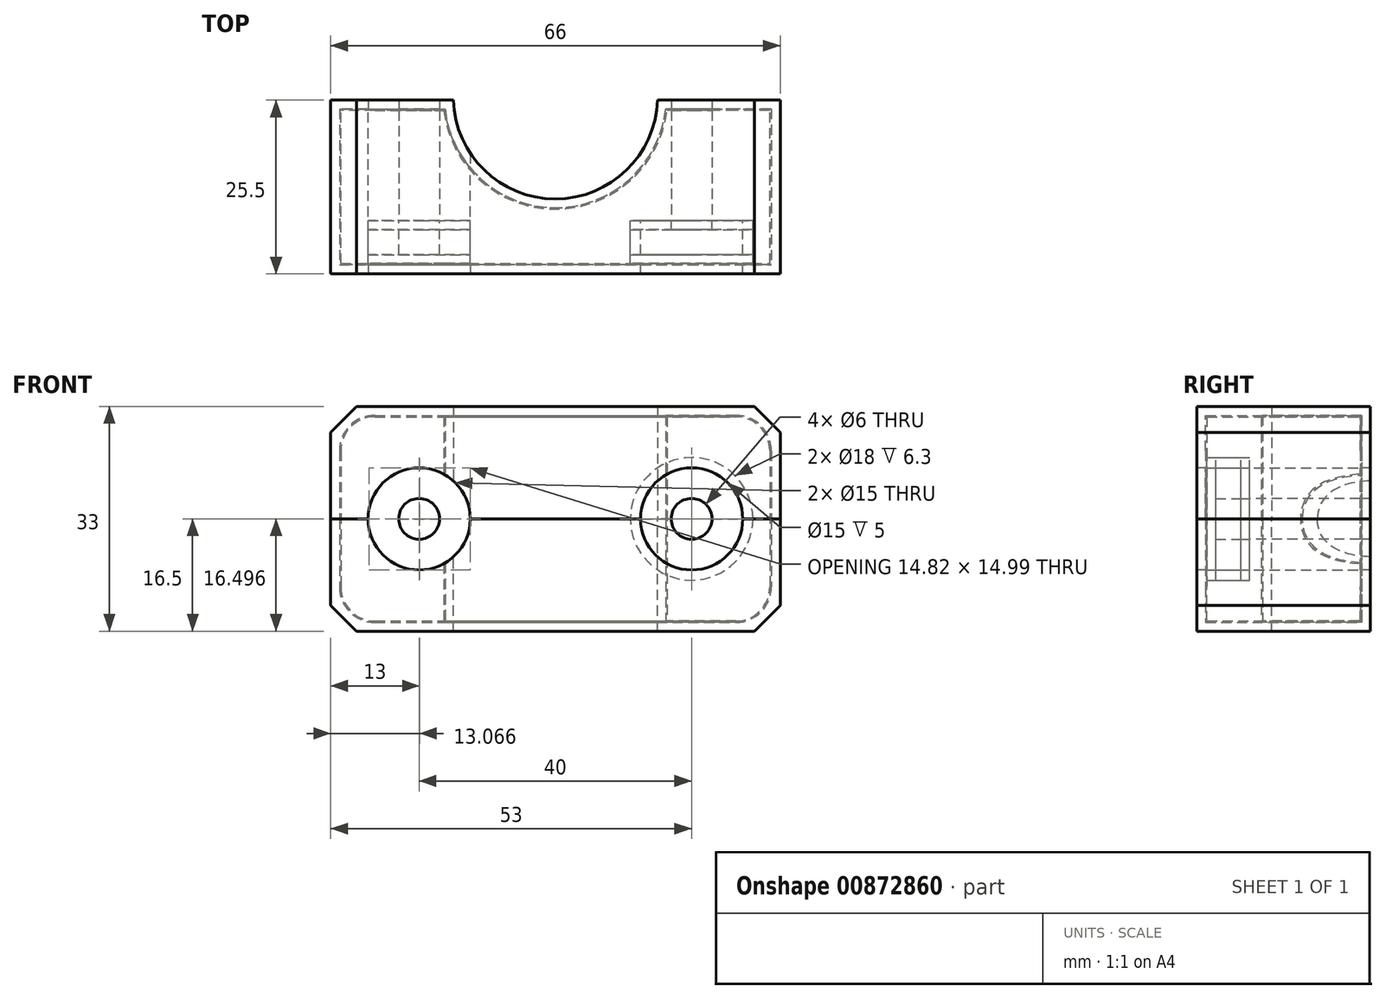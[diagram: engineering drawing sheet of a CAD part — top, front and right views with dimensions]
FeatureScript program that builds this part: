
annotation { "Feature Type Name" : "Feature", "Feature Type Description" : "" }
export const myFeature = defineFeature(function(context is Context, id is Id, definition is map)
    precondition{}
    {
        {
            assignVariable(context, id + "F0", {"name" : "Screw_head_height", "anyValue" : 5 * mm});
        }
        {
            assignVariable(context, id + "F1", {"name" : "Washer_height", "anyValue" : 1.3 * mm});
        }
        {
            assignVariable(context, id + "F2", {"name" : "rubber_thickness", "anyValue" : 1.5 * mm});
        }
        {
            assignVariable(context, id + "F3", {"name" : "width", "anyValue" : 30 * mm});
        }
        {
            assignVariable(context, id + "F4", {"name" : "cornerrad", "anyValue" : 5 * mm});
        }
        {
            assignVariable(context, id + "F5", {"name" : "carveout_offset", "anyValue" : 0.2 * mm});
        }
        {
            var Q0;
            Q0=qCreatedBy(makeId("Top.planeOp"),FACE);
            var sketch = newSketch(context, id + "F6", { "sketchPlane" : qUnion([Q0])});
            skLineSegment(sketch, "E0", {"start": v(-31.5, -6.3) * mm, "end": v(31.5, -6.3) * mm});
            skLineSegment(sketch, "E1", {"start": v(31.5, -6.3) * mm, "end": v(31.5, 16.2) * mm});
            skLineSegment(sketch, "E2", {"start": v(31.5, 16.2) * mm, "end": v(16.38, 16.2) * mm});
            skLineSegment(sketch, "E3", {"start": v(-31.5, -6.3) * mm, "end": v(-31.5, 16.2) * mm});
            skLineSegment(sketch, "E4", {"start": v(-31.5, 16.2) * mm, "end": v(-16.38, 16.2) * mm});
            skLineSegment(sketch, "E5", {"start": v(0, 0) * mm, "end": v(0, -6.3) * mm, "construction": true});
            skArc(sketch, "E6", {"start": v(-16.38, 16.2) * mm, "mid": v(0, 1.7) * mm, "end": v(16.38, 16.2) * mm});
            skLineSegment(sketch, "E7.0", {"start": v(-33, 17.7) * mm, "end": v(-15, 17.7) * mm});
            skLineSegment(sketch, "E7.1", {"start": v(33, 17.7) * mm, "end": v(15, 17.7) * mm});
            skLineSegment(sketch, "E7.2", {"start": v(33, -7.8) * mm, "end": v(33, 17.7) * mm});
            skArc(sketch, "E7.3", {"start": v(-15, 17.7) * mm, "mid": v(0, 3.2) * mm, "end": v(15, 17.7) * mm});
            skLineSegment(sketch, "E7.4", {"start": v(-33, -7.8) * mm, "end": v(33, -7.8) * mm});
            skLineSegment(sketch, "E7.5", {"start": v(-33, -7.8) * mm, "end": v(-33, 17.7) * mm});
            skSolve(sketch);
        }
        {
            var Q0;
            Q0=makeQuery(id+"F6.imprint","IMPRINT",FACE,{"disambiguationData":[TD([[makeQuery(id+"F6.imprint","IMPRINT",EDGE,{"derivedFrom":sQuery(id+"F6.wireOp",EDGE,"E0")}),1.0]])]});
            extrude(context, id + "F7", {"entities" : qUnion([Q0]), "depth" : getVariable(context, 'width') / 2, "offsetDistance" : 25 * mm, "hasSecondDirection" : true, "secondDirectionOppositeDirection" : true, "secondDirectionDepth" : getVariable(context, 'width') / 2});
        }
        {
            var Q0;
            Q0=makeQuery(id+"F6.imprint","IMPRINT",FACE,{"disambiguationData":[TD([[makeQuery(id+"F6.imprint","IMPRINT",EDGE,{"derivedFrom":sQuery(id+"F6.wireOp",EDGE,"E0")}),1.0]])]});
            extrude(context, id + "F8", {"entities" : qUnion([Q0]), "depth" : getVariable(context, 'width') / 2, "offsetDistance" : 25 * mm, "hasSecondDirection" : true, "secondDirectionOppositeDirection" : true, "secondDirectionDepth" : getVariable(context, 'width') / 2});
        }
        {
            var Q0;
            Q0=makeQuery(id+"F7.opExtrude","CAP_EDGE",EDGE,{"disambiguationData":[OSD([sQuery(id+"F6.wireOp",EDGE,"E1")])],"isStart":false});
            var Q1;
            Q1=makeQuery(id+"F7.opExtrude","CAP_EDGE",EDGE,{"disambiguationData":[OSD([sQuery(id+"F6.wireOp",EDGE,"E3")])],"isStart":false});
            var Q2;
            Q2=makeQuery(id+"F7.opExtrude","CAP_EDGE",EDGE,{"disambiguationData":[OSD([sQuery(id+"F6.wireOp",EDGE,"E1")])],"isStart":true});
            var Q3;
            Q3=makeQuery(id+"F7.opExtrude","CAP_EDGE",EDGE,{"disambiguationData":[OSD([sQuery(id+"F6.wireOp",EDGE,"E3")])],"isStart":true});
            var Q4;
            Q4=makeQuery(id+"F8.opExtrude","CAP_EDGE",EDGE,{"disambiguationData":[OSD([sQuery(id+"F6.wireOp",EDGE,"E3")])],"isStart":true});
            var Q5;
            Q5=makeQuery(id+"F8.opExtrude","CAP_EDGE",EDGE,{"disambiguationData":[OSD([sQuery(id+"F6.wireOp",EDGE,"E1")])],"isStart":true});
            var Q6;
            Q6=makeQuery(id+"F8.opExtrude","CAP_EDGE",EDGE,{"disambiguationData":[OSD([sQuery(id+"F6.wireOp",EDGE,"E3")])],"isStart":false});
            var Q7;
            Q7=makeQuery(id+"F8.opExtrude","CAP_EDGE",EDGE,{"disambiguationData":[OSD([sQuery(id+"F6.wireOp",EDGE,"E1")])],"isStart":false});
            fillet(context, id + "F9", {"entities" : qUnion([Q0, Q1, Q2, Q3, Q4, Q5, Q6, Q7]), "radius" : getVariable(context, 'cornerrad'), "tangentPropagation" : true, "allowEdgeOverflow" : false});
        }
        {
            var Q0;
            Q0=qCreatedBy(makeId("Front.planeOp"),FACE);
            var sketch = newSketch(context, id + "F10", { "sketchPlane" : qUnion([Q0])});
            skCircle(sketch, "E8", {"center": v(20, 0) * mm, "radius": 3 * mm});
            skLineSegment(sketch, "E9", {"start": v(0, 0) * mm, "end": v(20, 0) * mm, "construction": true});
            skCircle(sketch, "E10", {"center": v(20, 0) * mm, "radius": 9 * mm});
            skCircle(sketch, "E11", {"center": v(20, 0) * mm, "radius": 7.5 * mm});
            skCircle(sketch, "E12.MirrorC", {"center": v(-20, 0) * mm, "radius": 3 * mm});
            skCircle(sketch, "E13.MirrorC", {"center": v(-20, 0) * mm, "radius": 7.5 * mm});
            skCircle(sketch, "E14.MirrorC", {"center": v(-20, 0) * mm, "radius": 9 * mm});
            skLineSegment(sketch, "E15", {"start": v(-33, 16.5) * mm, "end": v(33, 16.5) * mm, "construction": true});
            skLineSegment(sketch, "E16", {"start": v(33, 16.5) * mm, "end": v(33, -16.5) * mm, "construction": true});
            skLineSegment(sketch, "E17", {"start": v(33, -16.5) * mm, "end": v(-33, -16.5) * mm, "construction": true});
            skLineSegment(sketch, "E18", {"start": v(-33, -16.5) * mm, "end": v(-33, 16.5) * mm, "construction": true});
            skLineSegment(sketch, "E19", {"start": v(-33, 12.7) * mm, "end": v(-29.2, 16.5) * mm});
            skLineSegment(sketch, "E20", {"start": v(0, 0) * mm, "end": v(0, 16.5) * mm, "construction": true});
            skLineSegment(sketch, "E21.MirrorCS", {"start": v(-45.7, 45.7) * mm, "end": v(-45.7, 65.7) * mm, "construction": true});
            skLineSegment(sketch, "E22", {"start": v(-29.2, 16.5) * mm, "end": v(-33, 16.5) * mm});
            skLineSegment(sketch, "E23", {"start": v(-33, 12.7) * mm, "end": v(-33, 16.5) * mm});
            skLineSegment(sketch, "E24.MirrorCS", {"start": v(33, 12.7) * mm, "end": v(29.2, 16.5) * mm});
            skLineSegment(sketch, "E25.MirrorCS", {"start": v(29.2, 16.5) * mm, "end": v(33, 16.5) * mm});
            skLineSegment(sketch, "E26.MirrorCS", {"start": v(33, 12.7) * mm, "end": v(33, 16.5) * mm});
            skLineSegment(sketch, "E27.MirrorCS", {"start": v(-29.2, -16.5) * mm, "end": v(-33, -16.5) * mm});
            skLineSegment(sketch, "E28.MirrorCS", {"start": v(-33, -12.7) * mm, "end": v(-29.2, -16.5) * mm});
            skLineSegment(sketch, "E29.MirrorCS", {"start": v(-33, -12.7) * mm, "end": v(-33, -16.5) * mm});
            skLineSegment(sketch, "E30.MirrorCS", {"start": v(29.2, -16.5) * mm, "end": v(33, -16.5) * mm});
            skLineSegment(sketch, "E31.MirrorCS", {"start": v(33, -12.7) * mm, "end": v(29.2, -16.5) * mm});
            skLineSegment(sketch, "E32.MirrorCS", {"start": v(33, -12.7) * mm, "end": v(33, -16.5) * mm});
            skSolve(sketch);
        }
        {
            var Q0;
            Q0=makeQuery(id+"F10.imprint","IMPRINT",FACE,{"disambiguationData":[TD([[makeQuery(id+"F10.imprint","IMPRINT",EDGE,{"derivedFrom":sQuery(id+"F10.wireOp",EDGE,"E12.MirrorC")}),1.0]])]});
            var Q1;
            Q1=makeQuery(id+"F10.imprint","IMPRINT",FACE,{"disambiguationData":[TD([[makeQuery(id+"F10.imprint","IMPRINT",EDGE,{"derivedFrom":sQuery(id+"F10.wireOp",EDGE,"E13.MirrorC")}),1.0]])]});
            var Q2;
            Q2=makeQuery(id+"F10.imprint","IMPRINT",FACE,{"disambiguationData":[TD([[makeQuery(id+"F10.imprint","IMPRINT",EDGE,{"derivedFrom":sQuery(id+"F10.wireOp",EDGE,"E8")}),-1.0]])]});
            var Q3;
            Q3=makeQuery(id+"F10.imprint","IMPRINT",FACE,{"disambiguationData":[TD([[makeQuery(id+"F10.imprint","IMPRINT",EDGE,{"derivedFrom":sQuery(id+"F10.wireOp",EDGE,"E10")}),1.0]])]});
            extrude(context, id + "F11", {"entities" : qUnion([Q0, Q1, Q2, Q3]), "operationType" : NewBodyOperationType.REMOVE, "depth" : getVariable(context, 'Screw_head_height') + getVariable(context, 'Washer_height'), "offsetDistance" : 25 * mm});
        }
        {
            var Q0;
            Q0=makeQuery(id+"F6.imprint","IMPRINT",FACE,{"disambiguationData":[TD([[makeQuery(id+"F6.imprint","IMPRINT",EDGE,{"derivedFrom":sQuery(id+"F6.wireOp",EDGE,"E0")}),-1.0]])]});
            var Q1;
            Q1=makeQuery(id+"F6.imprint","IMPRINT",FACE,{"disambiguationData":[TD([[makeQuery(id+"F6.imprint","IMPRINT",EDGE,{"derivedFrom":sQuery(id+"F6.wireOp",EDGE,"E0")}),1.0]])]});
            extrude(context, id + "F12", {"entities" : qUnion([Q0, Q1]), "depth" : getVariable(context, 'width') / 2 + getVariable(context, 'rubber_thickness'), "offsetDistance" : 25 * mm});
        }
        {
            var Q0;
            Q0=makeQuery(id+"F6.imprint","IMPRINT",FACE,{"disambiguationData":[TD([[makeQuery(id+"F6.imprint","IMPRINT",EDGE,{"derivedFrom":sQuery(id+"F6.wireOp",EDGE,"E0")}),-1.0]])]});
            var Q1;
            Q1=makeQuery(id+"F6.imprint","IMPRINT",FACE,{"disambiguationData":[TD([[makeQuery(id+"F6.imprint","IMPRINT",EDGE,{"derivedFrom":sQuery(id+"F6.wireOp",EDGE,"E0")}),1.0]])]});
            extrude(context, id + "F13", {"entities" : qUnion([Q0, Q1]), "oppositeDirection" : true, "depth" : getVariable(context, 'width') / 2 + getVariable(context, 'rubber_thickness'), "offsetDistance" : 25 * mm});
        }
        {
            var Q0;
            Q0=makeQuery(id+"F6.imprint","IMPRINT",FACE,{"disambiguationData":[TD([[makeQuery(id+"F6.imprint","IMPRINT",EDGE,{"derivedFrom":sQuery(id+"F6.wireOp",EDGE,"E0")}),-1.0]])]});
            var Q1;
            Q1=makeQuery(id+"F6.imprint","IMPRINT",FACE,{"disambiguationData":[TD([[makeQuery(id+"F6.imprint","IMPRINT",EDGE,{"derivedFrom":sQuery(id+"F6.wireOp",EDGE,"E0")}),1.0]])]});
            extrude(context, id + "F14", {"entities" : qUnion([Q0, Q1]), "depth" : getVariable(context, 'width') / 2 + getVariable(context, 'rubber_thickness'), "offsetDistance" : 25 * mm});
        }
        {
            var Q0;
            Q0=makeQuery(id+"F6.imprint","IMPRINT",FACE,{"disambiguationData":[TD([[makeQuery(id+"F6.imprint","IMPRINT",EDGE,{"derivedFrom":sQuery(id+"F6.wireOp",EDGE,"E0")}),-1.0]])]});
            var Q1;
            Q1=makeQuery(id+"F6.imprint","IMPRINT",FACE,{"disambiguationData":[TD([[makeQuery(id+"F6.imprint","IMPRINT",EDGE,{"derivedFrom":sQuery(id+"F6.wireOp",EDGE,"E0")}),1.0]])]});
            extrude(context, id + "F15", {"entities" : qUnion([Q0, Q1]), "oppositeDirection" : true, "depth" : getVariable(context, 'width') / 2 + getVariable(context, 'rubber_thickness'), "offsetDistance" : 25 * mm});
        }
        {
            var Q0;
            Q0=makeQuery(id+"F10.imprint","IMPRINT",FACE,{"disambiguationData":[TD([[makeQuery(id+"F10.imprint","IMPRINT",EDGE,{"derivedFrom":sQuery(id+"F10.wireOp",EDGE,"E12.MirrorC")}),-1.0]])]});
            var Q1;
            Q1=makeQuery(id+"F10.imprint","IMPRINT",FACE,{"disambiguationData":[TD([[makeQuery(id+"F10.imprint","IMPRINT",EDGE,{"derivedFrom":sQuery(id+"F10.wireOp",EDGE,"E8")}),1.0]])]});
            var Q2;
            Q2=makeQuery(id+"F15.opExtrude","SWEPT_FACE",FACE,{"disambiguationData":[OSD([sQuery(id+"F6.wireOp",EDGE,"E7.0")])]});
            var Q3;
            Q3=makeQuery(id+"F14.opExtrude","SWEPT_FACE",FACE,{"disambiguationData":[OSD([sQuery(id+"F6.wireOp",EDGE,"E7.4")])]});
            extrude(context, id + "F16", {"entities" : qUnion([Q0, Q1]), "operationType" : NewBodyOperationType.REMOVE, "endBound" : BoundingType.UP_TO_SURFACE, "oppositeDirection" : true, "depth" : 25 * mm, "endBoundEntityFace" : qUnion([Q2]), "offsetDistance" : 25 * mm, "hasSecondDirection" : true, "secondDirectionBound" : SecondDirectionBoundingType.UP_TO_SURFACE, "secondDirectionOppositeDirection" : false, "secondDirectionDepth" : 25 * mm, "secondDirectionBoundEntityFace" : qUnion([Q3])});
        }
        {
            var Q0;
            Q0=makeQuery(id+"F7.opExtrude","SWEPT_BODY",BODY,{"disambiguationData":[OSD([sQuery(id+"F6.wireOp",EDGE,"E0"),sQuery(id+"F6.wireOp",EDGE,"E1"),sQuery(id+"F6.wireOp",EDGE,"E2"),sQuery(id+"F6.wireOp",EDGE,"E3"),sQuery(id+"F6.wireOp",EDGE,"E4"),sQuery(id+"F6.wireOp",EDGE,"E6")])]});
            var Q1;
            Q1=makeQuery(id+"F12.opExtrude","SWEPT_BODY",BODY,{"disambiguationData":[OSD([sQuery(id+"F6.wireOp",EDGE,"E7.0"),sQuery(id+"F6.wireOp",EDGE,"E7.1"),sQuery(id+"F6.wireOp",EDGE,"E7.2"),sQuery(id+"F6.wireOp",EDGE,"E7.3"),sQuery(id+"F6.wireOp",EDGE,"E7.4"),sQuery(id+"F6.wireOp",EDGE,"E7.5")])]});
            var Q2;
            Q2=makeQuery(id+"F13.opExtrude","SWEPT_BODY",BODY,{"disambiguationData":[OSD([sQuery(id+"F6.wireOp",EDGE,"E7.0"),sQuery(id+"F6.wireOp",EDGE,"E7.1"),sQuery(id+"F6.wireOp",EDGE,"E7.2"),sQuery(id+"F6.wireOp",EDGE,"E7.3"),sQuery(id+"F6.wireOp",EDGE,"E7.4"),sQuery(id+"F6.wireOp",EDGE,"E7.5")])]});
            booleanBodies(context, id + "F17", {"operationType" : BooleanOperationType.SUBTRACTION, "tools" : qUnion([Q0]), "targets" : qUnion([Q1, Q2]), "offset" : true, "offsetAll" : true, "offsetDistance" : getVariable(context, 'carveout_offset'), "keepTools" : true});
        }
        {
            var Q0;
            Q0=makeQuery(id+"F8.opExtrude","SWEPT_BODY",BODY,{"disambiguationData":[OSD([sQuery(id+"F6.wireOp",EDGE,"E0"),sQuery(id+"F6.wireOp",EDGE,"E1"),sQuery(id+"F6.wireOp",EDGE,"E2"),sQuery(id+"F6.wireOp",EDGE,"E3"),sQuery(id+"F6.wireOp",EDGE,"E4"),sQuery(id+"F6.wireOp",EDGE,"E6")])]});
            var Q1;
            Q1=makeQuery(id+"F14.opExtrude","SWEPT_BODY",BODY,{"disambiguationData":[OSD([sQuery(id+"F6.wireOp",EDGE,"E7.0"),sQuery(id+"F6.wireOp",EDGE,"E7.1"),sQuery(id+"F6.wireOp",EDGE,"E7.2"),sQuery(id+"F6.wireOp",EDGE,"E7.3"),sQuery(id+"F6.wireOp",EDGE,"E7.4"),sQuery(id+"F6.wireOp",EDGE,"E7.5")])]});
            var Q2;
            Q2=makeQuery(id+"F15.opExtrude","SWEPT_BODY",BODY,{"disambiguationData":[OSD([sQuery(id+"F6.wireOp",EDGE,"E7.0"),sQuery(id+"F6.wireOp",EDGE,"E7.1"),sQuery(id+"F6.wireOp",EDGE,"E7.2"),sQuery(id+"F6.wireOp",EDGE,"E7.3"),sQuery(id+"F6.wireOp",EDGE,"E7.4"),sQuery(id+"F6.wireOp",EDGE,"E7.5")])]});
            booleanBodies(context, id + "F18", {"operationType" : BooleanOperationType.SUBTRACTION, "tools" : qUnion([Q0]), "targets" : qUnion([Q1, Q2]), "offset" : true, "offsetAll" : true, "offsetDistance" : getVariable(context, 'carveout_offset'), "keepTools" : true});
        }
        {
            var Q0;
            Q0=makeQuery(id+"F10.imprint","IMPRINT",FACE,{"disambiguationData":[TD([[makeQuery(id+"F10.imprint","IMPRINT",EDGE,{"derivedFrom":sQuery(id+"F10.wireOp",EDGE,"E19")}),1.0]])]});
            var Q1;
            Q1=makeQuery(id+"F10.imprint","IMPRINT",FACE,{"disambiguationData":[TD([[makeQuery(id+"F10.imprint","IMPRINT",EDGE,{"derivedFrom":sQuery(id+"F10.wireOp",EDGE,"E27.MirrorCS")}),-1.0]])]});
            var Q2;
            Q2=makeQuery(id+"F10.imprint","IMPRINT",FACE,{"disambiguationData":[TD([[makeQuery(id+"F10.imprint","IMPRINT",EDGE,{"derivedFrom":sQuery(id+"F10.wireOp",EDGE,"E30.MirrorCS")}),1.0]])]});
            var Q3;
            Q3=makeQuery(id+"F10.imprint","IMPRINT",FACE,{"disambiguationData":[TD([[makeQuery(id+"F10.imprint","IMPRINT",EDGE,{"derivedFrom":sQuery(id+"F10.wireOp",EDGE,"E24.MirrorCS")}),-1.0]])]});
            var Q4;
            Q4=makeQuery(id+"F14.opExtrude","SWEPT_FACE",FACE,{"disambiguationData":[OSD([sQuery(id+"F6.wireOp",EDGE,"E7.1")])]});
            var Q5;
            Q5=makeQuery(id+"F14.opExtrude","SWEPT_FACE",FACE,{"disambiguationData":[OSD([sQuery(id+"F6.wireOp",EDGE,"E7.4")])]});
            extrude(context, id + "F19", {"entities" : qUnion([Q0, Q1, Q2, Q3]), "operationType" : NewBodyOperationType.REMOVE, "endBound" : BoundingType.UP_TO_SURFACE, "oppositeDirection" : true, "depth" : 25 * mm, "endBoundEntityFace" : qUnion([Q4]), "offsetDistance" : 25 * mm, "hasSecondDirection" : true, "secondDirectionBound" : SecondDirectionBoundingType.UP_TO_SURFACE, "secondDirectionOppositeDirection" : false, "secondDirectionDepth" : 25 * mm, "secondDirectionBoundEntityFace" : qUnion([Q5])});
        }
        {
            var Q0;
            Q0=makeQuery(id+"F10.imprint","IMPRINT",FACE,{"disambiguationData":[TD([[makeQuery(id+"F10.imprint","IMPRINT",EDGE,{"derivedFrom":sQuery(id+"F10.wireOp",EDGE,"E13.MirrorC")}),1.0]])]});
            var Q1;
            Q1=makeQuery(id+"F10.imprint","IMPRINT",FACE,{"disambiguationData":[TD([[makeQuery(id+"F10.imprint","IMPRINT",EDGE,{"derivedFrom":sQuery(id+"F10.wireOp",EDGE,"E12.MirrorC")}),1.0]])]});
            var Q2;
            Q2=makeQuery(id+"F10.imprint","IMPRINT",FACE,{"disambiguationData":[TD([[makeQuery(id+"F10.imprint","IMPRINT",EDGE,{"derivedFrom":sQuery(id+"F10.wireOp",EDGE,"E10")}),1.0]])]});
            var Q3;
            Q3=makeQuery(id+"F10.imprint","IMPRINT",FACE,{"disambiguationData":[TD([[makeQuery(id+"F10.imprint","IMPRINT",EDGE,{"derivedFrom":sQuery(id+"F10.wireOp",EDGE,"E8")}),-1.0]])]});
            var Q4;
            {var subQ4=sQuery(id+"F6.wireOp",EDGE,"E1");var subQ5=sQuery(id+"F6.wireOp",EDGE,"E0");var subQ8=makeQuery(id+"F9.opFillet","BLEND_FACE",FACE,{"disambiguationData":[OSD([subQ4]),TDD([makeQuery(id+"F7.opExtrude","CAP_EDGE",EDGE,{"disambiguationData":[OSD([subQ4])],"isStart":false})])]});var subQ10=makeQuery(id+"F7.opExtrude","SWEPT_FACE",FACE,{"disambiguationData":[OSD([subQ4])]});Q4=makeQuery(id+"F17.tempBoolean.opBoolean","COPY",FACE,{"disambiguationData":[TD([makeQuery(id+"F17.offsetTempBody.opPattern","COPY",FACE,{"derivedFrom":subQ8,"instanceName":"1"})])],"derivedFrom":makeQuery(id+"F17.offsetTempBody.opPattern","COPY",FACE,{"derivedFrom":makeQuery(id+"F11.boolean.opBoolean","SPLIT",FACE,{"disambiguationData":[TD([subQ10])],"derivedFrom":makeQuery(id+"F7.opExtrude","SWEPT_FACE",FACE,{"disambiguationData":[OSD([subQ5])]})}),"instanceName":"1"})});}
            extrude(context, id + "F20", {"entities" : qUnion([Q0, Q1, Q2, Q3]), "operationType" : NewBodyOperationType.REMOVE, "endBound" : BoundingType.UP_TO_SURFACE, "depth" : 25 * mm, "endBoundEntityFace" : qUnion([Q4]), "offsetDistance" : 25 * mm});
        }
        {
            var Q0;
            Q0=makeQuery(id+"F10.imprint","IMPRINT",FACE,{"disambiguationData":[TD([[makeQuery(id+"F10.imprint","IMPRINT",EDGE,{"derivedFrom":sQuery(id+"F10.wireOp",EDGE,"E12.MirrorC")}),1.0]])]});
            var Q1;
            Q1=makeQuery(id+"F10.imprint","IMPRINT",FACE,{"disambiguationData":[TD([[makeQuery(id+"F10.imprint","IMPRINT",EDGE,{"derivedFrom":sQuery(id+"F10.wireOp",EDGE,"E8")}),-1.0]])]});
            var Q2;
            Q2=makeQuery(id+"F12.opExtrude","SWEPT_FACE",FACE,{"disambiguationData":[OSD([sQuery(id+"F6.wireOp",EDGE,"E7.4")])]});
            extrude(context, id + "F21", {"entities" : qUnion([Q0, Q1]), "operationType" : NewBodyOperationType.REMOVE, "endBound" : BoundingType.UP_TO_SURFACE, "depth" : 25 * mm, "endBoundEntityFace" : qUnion([Q2]), "offsetDistance" : 25 * mm});
        }
        {
            var Q0;
            Q0=makeQuery(id+"F10.imprint","IMPRINT",FACE,{"disambiguationData":[TD([[makeQuery(id+"F10.imprint","IMPRINT",EDGE,{"derivedFrom":sQuery(id+"F10.wireOp",EDGE,"E13.MirrorC")}),1.0]])]});
            var Q1;
            Q1=makeQuery(id+"F10.imprint","IMPRINT",FACE,{"disambiguationData":[TD([[makeQuery(id+"F10.imprint","IMPRINT",EDGE,{"derivedFrom":sQuery(id+"F10.wireOp",EDGE,"E12.MirrorC")}),1.0]])]});
            var Q2;
            Q2=makeQuery(id+"F10.imprint","IMPRINT",FACE,{"disambiguationData":[TD([[makeQuery(id+"F10.imprint","IMPRINT",EDGE,{"derivedFrom":sQuery(id+"F10.wireOp",EDGE,"E10")}),1.0]])]});
            var Q3;
            Q3=makeQuery(id+"F10.imprint","IMPRINT",FACE,{"disambiguationData":[TD([[makeQuery(id+"F10.imprint","IMPRINT",EDGE,{"derivedFrom":sQuery(id+"F10.wireOp",EDGE,"E8")}),-1.0]])]});
            extrude(context, id + "F22", {"entities" : qUnion([Q0, Q1, Q2, Q3]), "depth" : getVariable(context, 'Washer_height'), "offsetDistance" : 25 * mm});
        }
        {
            var Q0;
            Q0=makeQuery(id+"F10.imprint","IMPRINT",FACE,{"disambiguationData":[TD([[makeQuery(id+"F10.imprint","IMPRINT",EDGE,{"derivedFrom":sQuery(id+"F10.wireOp",EDGE,"E13.MirrorC")}),1.0]])]});
            var Q1;
            Q1=makeQuery(id+"F10.imprint","IMPRINT",FACE,{"disambiguationData":[TD([[makeQuery(id+"F10.imprint","IMPRINT",EDGE,{"derivedFrom":sQuery(id+"F10.wireOp",EDGE,"E10")}),1.0]])]});
            extrude(context, id + "F23", {"entities" : qUnion([Q0, Q1]), "depth" : getVariable(context, 'Screw_head_height'), "offsetDistance" : 25 * mm});
        }
    });
